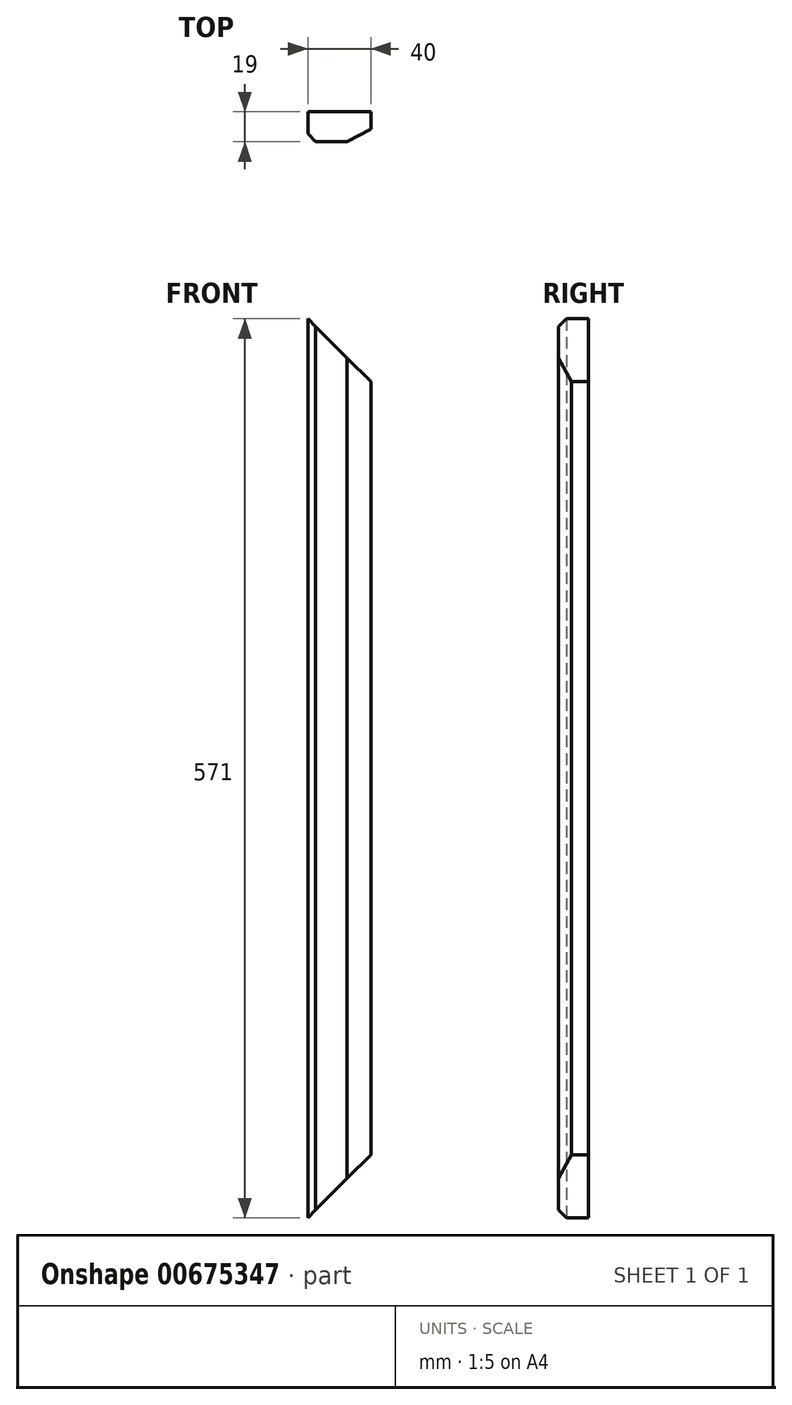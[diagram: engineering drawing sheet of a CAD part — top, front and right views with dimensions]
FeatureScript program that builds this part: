
annotation { "Feature Type Name" : "Feature", "Feature Type Description" : "" }
export const myFeature = defineFeature(function(context is Context, id is Id, definition is map)
    precondition{}
    {
        {
            var Q0;
            Q0=qCreatedBy(makeId("Top.planeOp"),FACE);
            var sketch = newSketch(context, id + "F0", { "sketchPlane" : qUnion([Q0])});
            skLineSegment(sketch, "E0", {"start": v(0, 0) * mm, "end": v(40, 0) * mm});
            skLineSegment(sketch, "E1", {"start": v(40, 0) * mm, "end": v(40, -11) * mm});
            skLineSegment(sketch, "E2", {"start": v(40, -11) * mm, "end": v(25, -19) * mm});
            skLineSegment(sketch, "E3", {"start": v(25, -19) * mm, "end": v(5, -19) * mm});
            skLineSegment(sketch, "E4", {"start": v(5, -19) * mm, "end": v(0, -14) * mm});
            skLineSegment(sketch, "E5", {"start": v(0, -14) * mm, "end": v(0, 0) * mm});
            skSolve(sketch);
        }
        {
            var Q0;
            Q0 = qSketchRegion(id + "F0", true);
            extrude(context, id + "F1", {"entities" : qUnion([Q0]), "depth" : 571 * mm, "offsetDistance" : 25 * mm});
        }
        {
            var Q0;
            Q0=qCreatedBy(makeId("Front.planeOp"),FACE);
            var sketch = newSketch(context, id + "F2", { "sketchPlane" : qUnion([Q0])});
            skLineSegment(sketch, "E6", {"start": v(0, 0) * mm, "end": v(0, 571) * mm, "construction": true});
            skLineSegment(sketch, "E7", {"start": v(0, 285.5) * mm, "end": v(54.96, 285.5) * mm, "construction": true});
            skLineSegment(sketch, "E8", {"start": v(0, 0) * mm, "end": v(40, 0) * mm});
            skLineSegment(sketch, "E9", {"start": v(40, 0) * mm, "end": v(40, 40) * mm});
            skLineSegment(sketch, "E10", {"start": v(40, 40) * mm, "end": v(0, 0) * mm});
            skLineSegment(sketch, "E11.MirrorCS", {"start": v(40, 531) * mm, "end": v(0, 571) * mm});
            skLineSegment(sketch, "E12.MirrorCS", {"start": v(40, 571) * mm, "end": v(40, 531) * mm});
            skLineSegment(sketch, "E13.MirrorCS", {"start": v(0, 571) * mm, "end": v(40, 571) * mm});
            skSolve(sketch);
        }
        {
            var Q0;
            Q0 = qSketchRegion(id + "F2", true);
            extrude(context, id + "F3", {"entities" : qUnion([Q0]), "operationType" : NewBodyOperationType.REMOVE, "depth" : 25 * mm, "offsetDistance" : 25 * mm});
        }
    });
